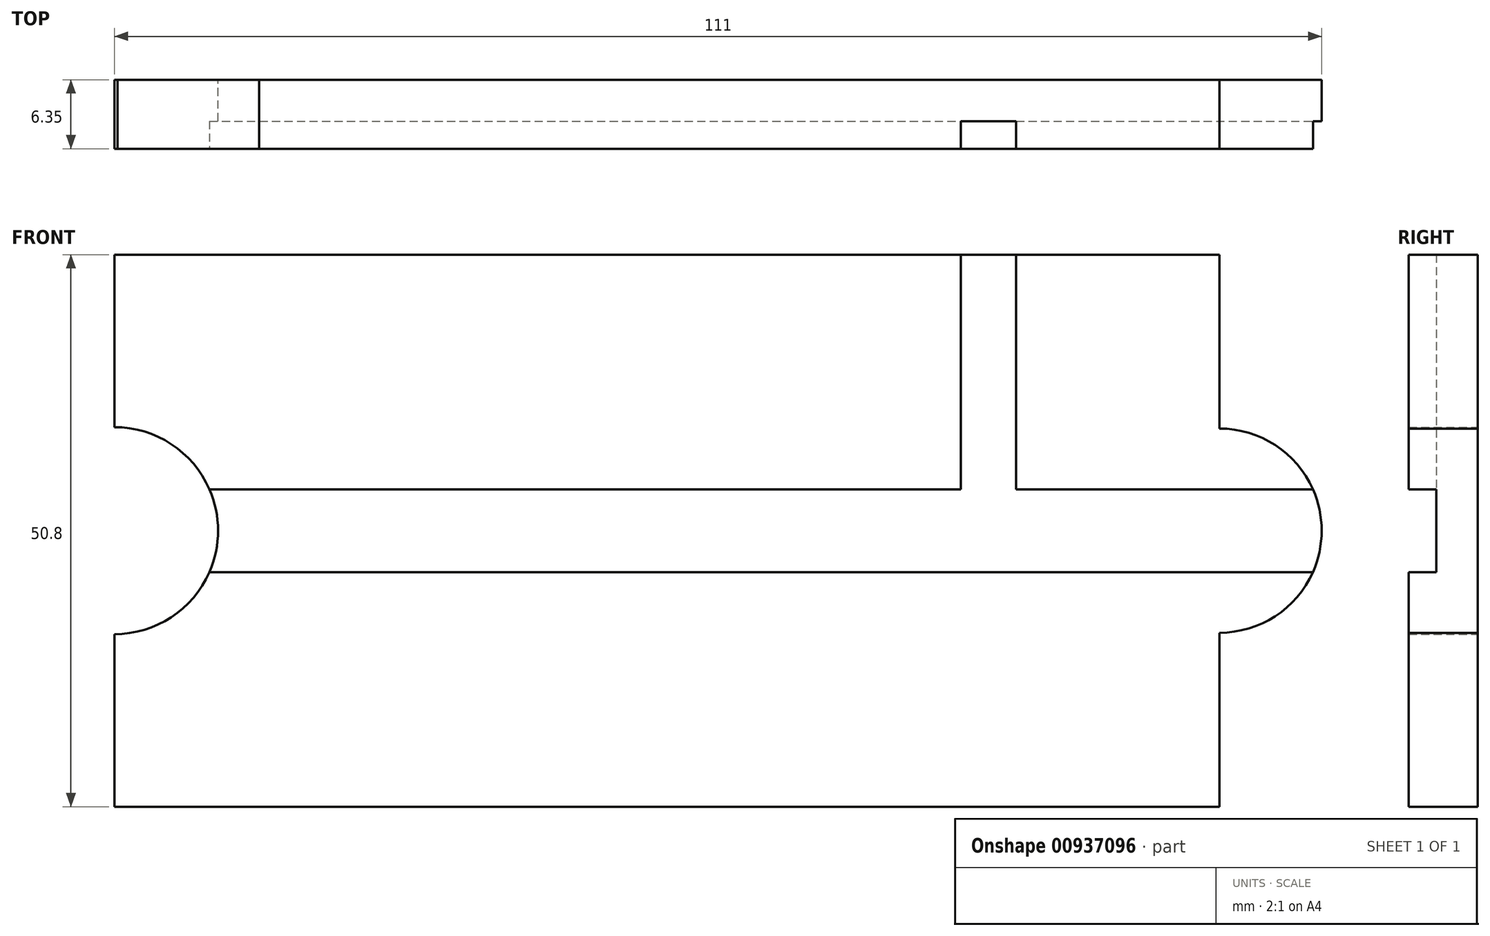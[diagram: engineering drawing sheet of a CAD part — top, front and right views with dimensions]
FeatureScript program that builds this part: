
annotation { "Feature Type Name" : "Feature", "Feature Type Description" : "" }
export const myFeature = defineFeature(function(context is Context, id is Id, definition is map)
    precondition{}
    {
        {
            var Q0;
            Q0=qCreatedBy(makeId("Front.planeOp"),FACE);
            var sketch = newSketch(context, id + "F0", { "sketchPlane" : qUnion([Q0])});
            skText(sketch, "E0", { "text": "A", "fontName": "Arimo-Regular.ttf"});
            skLineSegment(sketch, "E1", {"start": v(-49.5, -48.54) * mm, "end": v(-49.5, -64.41) * mm});
            skLineSegment(sketch, "E2", {"start": v(-49.5, -99.34) * mm, "end": v(52.1, -99.34) * mm});
            skLineSegment(sketch, "E3", {"start": v(52.1, -99.34) * mm, "end": v(52.1, -83.34) * mm});
            skArc(sketch, "E4", {"start": v(-49.5, -83.46) * mm, "mid": v(-39.98, -73.94) * mm, "end": v(-49.5, -64.41) * mm});
            skArc(sketch, "E5", {"start": v(52.1, -83.34) * mm, "mid": v(61.49, -73.94) * mm, "end": v(52.1, -64.54) * mm});
            skLineSegment(sketch, "E6.trimOffspring", {"start": v(-49.5, -83.46) * mm, "end": v(-49.5, -99.34) * mm});
            skLineSegment(sketch, "E7.trimOffspring", {"start": v(52.1, -64.54) * mm, "end": v(52.1, -48.54) * mm});
            skCircle(sketch, "E8", {"center": v(-39.68, -41.14) * mm, "radius": 3.5 * mm});
            skCircle(sketch, "E9", {"center": v(30.85, -41.14) * mm, "radius": 3.5 * mm});
            skCircle(sketch, "E10", {"center": v(-4.37, -16.22) * mm, "radius": 3.5 * mm});
            skLineSegment(sketch, "E11", {"start": v(-49.5, -48.54) * mm, "end": v(52.1, -48.54) * mm});
            const initialGuessF0  = {"E0": [-0.0495, -0.04854, 1, 0, 0.09708]};
            skSetInitialGuess(sketch, initialGuessF0);
            skSolve(sketch);
        }
        {
            var Q0;
            Q0=makeQuery(id+"F0.imprint","IMPRINT",FACE,{"disambiguationData":[TD([[makeQuery(id+"F0.imprint","IMPRINT",EDGE,{"derivedFrom":sQuery(id+"F0.wireOp",EDGE,"E0.sketch_text.stroke-0")}),-1.0]])]});
            var Q1;
            {var subQ3=sQuery(id+"F0.wireOp",EDGE,"E0.sketch_text.stroke-3");Q1=makeQuery(id+"F0.imprint","IMPRINT",FACE,{"disambiguationData":[TD([[makeQuery(id+"F0.imprint","IMPRINT",EDGE,{"derivedFrom":subQ3}),1.0]])]});}
            extrude(context, id + "F1", {"entities" : qUnion([Q0, Q1]), "depth" : 6.35 * mm, "offsetDistance" : 25.4 * mm});
        }
        {
            var Q0;
            Q0=makeQuery(id+"F1.opExtrude","CAP_FACE",FACE,{"disambiguationData":[OSD([sQuery(id+"F0.wireOp",EDGE,"E0.sketch_text.stroke-0"),sQuery(id+"F0.wireOp",EDGE,"E0.sketch_text.stroke-1"),sQuery(id+"F0.wireOp",EDGE,"E0.sketch_text.stroke-2"),sQuery(id+"F0.wireOp",EDGE,"E0.sketch_text.stroke-4"),sQuery(id+"F0.wireOp",EDGE,"E0.sketch_text.stroke-5"),sQuery(id+"F0.wireOp",EDGE,"E0.sketch_text.stroke-6"),sQuery(id+"F0.wireOp",EDGE,"E0.sketch_text.stroke-8"),sQuery(id+"F0.wireOp",EDGE,"E0.sketch_text.stroke-9"),sQuery(id+"F0.wireOp",EDGE,"E0.sketch_text.stroke-10"),sQuery(id+"F0.wireOp",EDGE,"E0.sketch_text.stroke-11"),sQuery(id+"F0.wireOp",EDGE,"E0.sketch_text.stroke-12"),sQuery(id+"F0.wireOp",EDGE,"E0.sketch_text.stroke-13"),sQuery(id+"F0.wireOp",EDGE,"E0.sketch_text.stroke-14"),sQuery(id+"F0.wireOp",EDGE,"E1"),sQuery(id+"F0.wireOp",EDGE,"E2"),sQuery(id+"F0.wireOp",EDGE,"E3"),sQuery(id+"F0.wireOp",EDGE,"E4"),sQuery(id+"F0.wireOp",EDGE,"E5"),sQuery(id+"F0.wireOp",EDGE,"E6.trimOffspring"),sQuery(id+"F0.wireOp",EDGE,"E7.trimOffspring"),sQuery(id+"F0.wireOp",EDGE,"E8"),sQuery(id+"F0.wireOp",EDGE,"E9"),sQuery(id+"F0.wireOp",EDGE,"E10"),sQuery(id+"F0.wireOp",EDGE,"E11")])],"isStart":false});
            var sketch = newSketch(context, id + "F2", { "sketchPlane" : qUnion([Q0])});
            skLineSegment(sketch, "E12", {"start": v(30.85, -41.14) * mm, "end": v(20.6, -16.22) * mm, "construction": true});
            skLineSegment(sketch, "E13", {"start": v(-39.68, -41.14) * mm, "end": v(-28.96, -15.32) * mm, "construction": true});
            skLineSegment(sketch, "E14", {"start": v(-32.09, -16.22) * mm, "end": v(20.6, -16.22) * mm, "construction": true});
            skLineSegment(sketch, "E15.0", {"start": v(33.2, -40.17) * mm, "end": v(22.3, -13.68) * mm});
            skLineSegment(sketch, "E16.0", {"start": v(-31.03, -13.68) * mm, "end": v(22.3, -13.68) * mm});
            skLineSegment(sketch, "E17.0", {"start": v(-27.64, -18.76) * mm, "end": v(18.9, -18.76) * mm});
            skLineSegment(sketch, "E18.0", {"start": v(-31.03, -13.68) * mm, "end": v(-42.03, -40.17) * mm});
            skLineSegment(sketch, "E19.0", {"start": v(-27.64, -18.76) * mm, "end": v(-37.34, -42.11) * mm});
            skPoint(sketch, "E20.orphan", {"position": v(-4.37, -16.22) * mm});
            skLineSegment(sketch, "E21.0", {"start": v(28.5, -42.1) * mm, "end": v(18.9, -18.76) * mm});
            skLineSegment(sketch, "E22", {"start": v(-49.5, -73.94) * mm, "end": v(63.39, -73.94) * mm, "construction": true});
            skLineSegment(sketch, "E23.0", {"start": v(-49.5, -77.75) * mm, "end": v(63.6, -77.75) * mm});
            skLineSegment(sketch, "E24.0", {"start": v(-49.5, -70.13) * mm, "end": v(28.31, -70.13) * mm});
            skPoint(sketch, "E25.orphan", {"position": v(52.1, -73.94) * mm});
            skPoint(sketch, "E26.trimOffspring.end.orphan", {"position": v(-4.25, 44.22) * mm});
            skLineSegment(sketch, "E27", {"start": v(30.85, -41.14) * mm, "end": v(30.85, -70.13) * mm, "construction": true});
            skLineSegment(sketch, "E28.0", {"start": v(28.31, -41.14) * mm, "end": v(28.31, -70.13) * mm});
            skLineSegment(sketch, "E29.0", {"start": v(33.4, -41.14) * mm, "end": v(33.4, -70.13) * mm});
            skLineSegment(sketch, "E30.trimOffspring", {"start": v(33.4, -70.13) * mm, "end": v(63.19, -70.13) * mm});
            skLineSegment(sketch, "E31", {"start": v(-49.5, -70.13) * mm, "end": v(-49.5, -77.75) * mm});
            skLineSegment(sketch, "E32", {"start": v(63.19, -70.13) * mm, "end": v(63.6, -77.75) * mm});
            skLineSegment(sketch, "E33", {"start": v(-42.03, -40.17) * mm, "end": v(-37.34, -42.11) * mm});
            skSolve(sketch);
        }
        {
            var Q0;
            {var subQ0=sQuery(id+"F2.wireOp",EDGE,"E18.0");var subQ1=sQuery(id+"F2.wireOp",EDGE,"E16.0");var subQ2=makeQuery(id+"F2.imprint","INTERSECT",VERTEX,{"derivedFrom":[subQ1,subQ0]});Q0=makeQuery(id+"F2.imprint","IMPRINT",FACE,{"disambiguationData":[TD([[makeQuery(id+"F2.imprint","IMPRINT",EDGE,{"disambiguationData":[TD([[subQ2,-1.0]])],"derivedFrom":subQ1}),-1.0]])]});}
            var Q1;
            {var subQ5=sQuery(id+"F2.wireOp",EDGE,"E15.0");var subQ9=sQuery(id+"F2.wireOp",EDGE,"E16.0");var subQ11=makeQuery(id+"F2.imprint","INTERSECT",VERTEX,{"derivedFrom":[subQ5,subQ9]});Q1=makeQuery(id+"F2.imprint","IMPRINT",FACE,{"disambiguationData":[TD([[makeQuery(id+"F2.imprint","IMPRINT",EDGE,{"disambiguationData":[TD([[subQ11,1.0]])],"derivedFrom":subQ5}),1.0]])]});}
            var Q2;
            {var subQ8=makeQuery(id+"F1.opExtrude","CAP_EDGE",EDGE,{"disambiguationData":[OSD([sQuery(id+"F0.wireOp",EDGE,"E4")])],"isStart":false});var subQ11=sQuery(id+"F2.wireOp",EDGE,"E23.0");var subQ15=makeQuery(id+"F2.imprint","INTERSECT",VERTEX,{"derivedFrom":[subQ8,subQ11]});Q2=makeQuery(id+"F2.imprint","IMPRINT",FACE,{"disambiguationData":[TD([[makeQuery(id+"F2.imprint","IMPRINT",EDGE,{"disambiguationData":[TD([[subQ15,-1.0]])],"derivedFrom":subQ11}),1.0]])]});}
            extrude(context, id + "F3", {"entities" : qUnion([Q0, Q1, Q2]), "operationType" : NewBodyOperationType.REMOVE, "oppositeDirection" : true, "depth" : 2.54 * mm, "offsetDistance" : 25.4 * mm});
        }
    });
